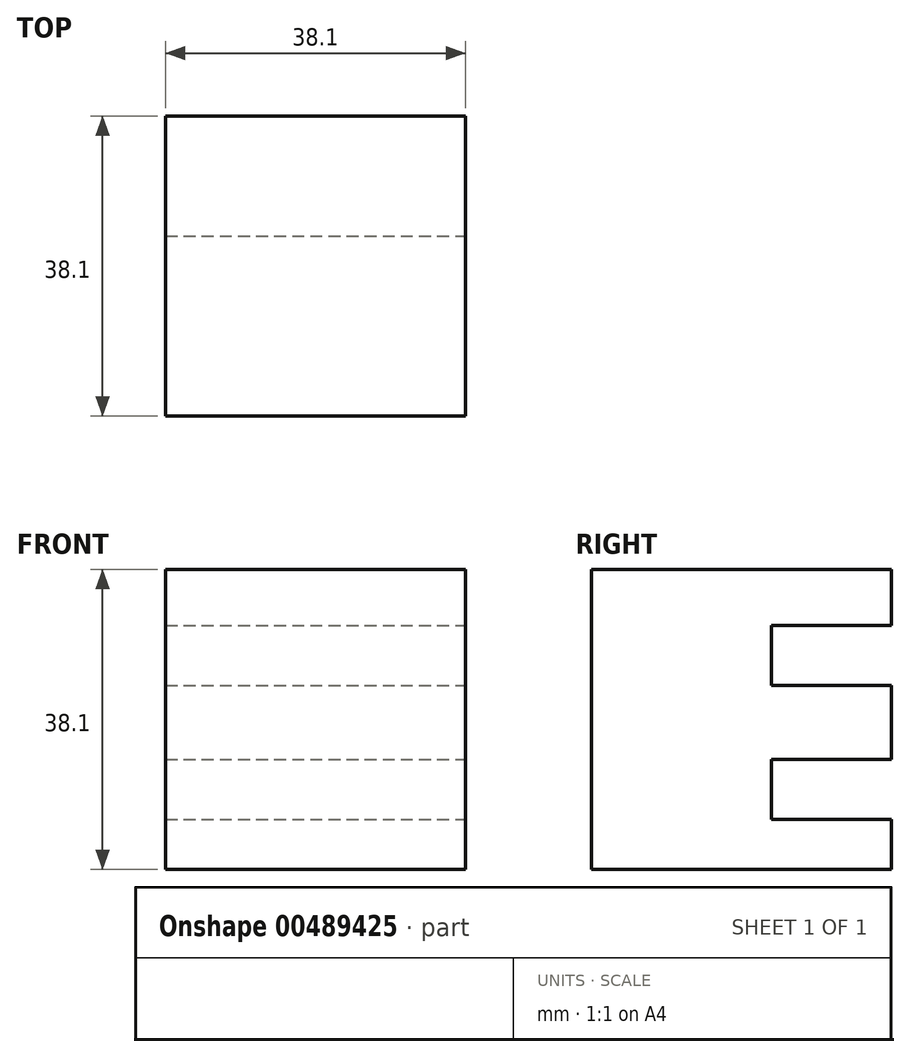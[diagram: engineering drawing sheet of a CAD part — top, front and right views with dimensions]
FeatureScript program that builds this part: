
annotation { "Feature Type Name" : "Feature", "Feature Type Description" : "" }
export const myFeature = defineFeature(function(context is Context, id is Id, definition is map)
    precondition{}
    {
        {
            var Q0;
            Q0=qCreatedBy(makeId("Front.planeOp"),FACE);
            var sketch = newSketch(context, id + "F0", { "sketchPlane" : qUnion([Q0])});
            skLineSegment(sketch, "E0.bottom", {"start": v(0, 0) * mm, "end": v(38.1, 0) * mm});
            skLineSegment(sketch, "E0.top", {"start": v(0, 38.1) * mm, "end": v(38.1, 38.1) * mm});
            skLineSegment(sketch, "E0.left", {"start": v(0, 0) * mm, "end": v(0, 38.1) * mm});
            skLineSegment(sketch, "E0.right", {"start": v(38.1, 0) * mm, "end": v(38.1, 38.1) * mm});
            skSolve(sketch);
        }
        {
            var Q0;
            Q0 = qSketchRegion(id + "F0", true);
            extrude(context, id + "F1", {"entities" : qUnion([Q0]), "depth" : 38.1 * mm, "offsetDistance" : 25.4 * mm});
        }
        {
            var Q0;
            Q0=qCreatedBy(makeId("Right.planeOp"),FACE);
            cPlane(context, id + "F2", {"entities" : qUnion([Q0]), "cplaneType" : CPlaneType.OFFSET, "offset" : 38.1 * mm, "width" : 152.4 * mm, "height" : 152.4 * mm});
        }
        {
            var Q0;
            Q0=qCreatedBy(id+"F2.planeOp",FACE);
            var sketch = newSketch(context, id + "F3", { "sketchPlane" : qUnion([Q0])});
            skLineSegment(sketch, "E1", {"start": v(-38.1, 38.1) * mm, "end": v(0, 38.1) * mm});
            skLineSegment(sketch, "E2", {"start": v(0, 38.1) * mm, "end": v(0, 0) * mm});
            skLineSegment(sketch, "E3", {"start": v(0, 0) * mm, "end": v(-38.1, 0) * mm});
            skLineSegment(sketch, "E4", {"start": v(-38.1, 0) * mm, "end": v(-38.1, 38.1) * mm});
            skLineSegment(sketch, "E5", {"start": v(0, 38.1) * mm, "end": v(-38.1, 38.1) * mm});
            skLineSegment(sketch, "E6", {"start": v(0, 31) * mm, "end": v(-15.24, 31) * mm});
            skLineSegment(sketch, "E7", {"start": v(-15.24, 23.38) * mm, "end": v(0, 23.38) * mm});
            skLineSegment(sketch, "E8", {"start": v(-15.24, 31) * mm, "end": v(-15.24, 23.38) * mm});
            skLineSegment(sketch, "E9", {"start": v(0, 14) * mm, "end": v(-15.24, 14) * mm});
            skLineSegment(sketch, "E10", {"start": v(-15.24, 14) * mm, "end": v(-15.24, 6.39) * mm});
            skLineSegment(sketch, "E11", {"start": v(-15.24, 6.39) * mm, "end": v(0, 6.39) * mm});
            skSolve(sketch);
        }
        {
            var Q0;
            {var subQ0=sQuery(id+"F3.wireOp",EDGE,"E6");Q0=makeQuery(id+"F3.imprint","IMPRINT",FACE,{"disambiguationData":[TD([[makeQuery(id+"F3.imprint","IMPRINT",EDGE,{"derivedFrom":subQ0}),1.0]])]});}
            var Q1;
            {var subQ0=sQuery(id+"F3.wireOp",EDGE,"E9");Q1=makeQuery(id+"F3.imprint","IMPRINT",FACE,{"disambiguationData":[TD([[makeQuery(id+"F3.imprint","IMPRINT",EDGE,{"derivedFrom":subQ0}),1.0]])]});}
            extrude(context, id + "F4", {"entities" : qUnion([Q0, Q1]), "operationType" : NewBodyOperationType.REMOVE, "oppositeDirection" : true, "depth" : 38.1 * mm, "offsetDistance" : 25.4 * mm});
        }
    });
